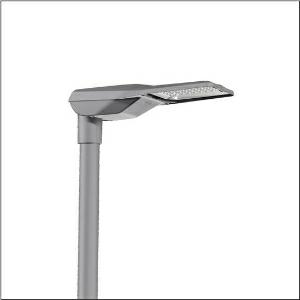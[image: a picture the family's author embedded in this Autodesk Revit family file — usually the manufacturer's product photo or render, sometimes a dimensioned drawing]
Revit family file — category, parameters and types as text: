
# Revit family: streetlight_sl_21_iq_mini___st1_0a_5xe2d31g08hb_3bda
name_source: partatom
category: Lighting Fixtures
units: mm (PartAtom-declared; Revit-internal decimal feet)

## family parameters
Cut with Voids When Loaded = No
Host = Face
Light Source = No
Part Type = Normal
Room Calculation Point = No
Round Connector Dimension = Use Diameter
Shared = No

## types (1)
- --- (1 x LED, 9450 lm, 70.9 W, 3000K)
    Apparent Load = 71 VA
    CIE Flux Codes = 37 72 97 100 100
    Color Rendering = 70
    Color Temperature = 3000K
    Default Elevation = 1800 mm
    Description = Streetlight SL 21 iQ mini, mast luminaire, primary light control with lens, of PMMA, primary optical cover: cover, of toughened safety glass, transparent, light distribution: ST1.0a, light emission: direct distribution, primary light characteristic: asymmetric, installation type: post-top, side-entry, LED, High Power LED, rated luminous flux: 9.450lm, luminous efficacy: 133lm/W, light colour: 730, colour temperature: 3000K, control gear: iQ Street-Remote, control: Street-Remote, Auto-Match, Temp-Guard, Lumen-Switch, Night-Set, Smart-Wire, Light-Fading, Desk-Remote (wireless, voltage-free reading and setting of iQ features in the workshop via application-optimized NFC function/RFID function), optimised constant luminous flux control (CLO 2.0), pre-setting: linear dimming characteristic, mains connection: 220..240V, AC, 50/60Hz, start of lifetime: 71W, end of service life: 75W, reduction: 31W, luminaire housing, of diecast aluminium, powder-coated, Siteco® metallic grey (DB 702S), corrosivity category C5 mid according to DIN EN ISO 12944, please order mast flange separately, inclination adjustable: 0°, 5°, 10°, 15°, sealing non-destructively replaceable, multi-level sealing system, length: 628mm, width: 235mm, height: 110mm, mast flange for spigot size: 42mm (side-entry): 5XC10008XM4, 60/48mm (side-entry/post-top): 5XC10108XM2, 76/60mm (side-entry/post-top): 5XC10108XM1, mounting height: 4..8m, protection rating (complete): IP66, insulation class (complete): insulation class II (safety insulation), certification: CE, ENEC, ENEC+, VDE, impact resistance: IK10, permissible operating ambient temperature for outdoor applications: -40..+50°C, standard-compliant lighting for roads and squares, packaging unit: 1 piece

Light Distribution: ST1.0a
    Height = 110 mm
    Lamp = 1 x LED
    Lamp Light Flux = 9450 lm
    Lamp Power = 70.9 W
    Lamp count = 1
    Length = 625 mm
    Luminous efficacy = 133 lm/W
    Manufacturer = Siteco
    ModVariant = No
    Model = 5XE2D31G08HB
    Number of Poles = 1
    OnlyDefault = Yes
    Power Factor = 1
    Product Name = Streetlight SL 21 iQ mini | ST1.0a
    Product group = mast luminaire | pylon top
    ProductGroupID = 6100
    Protection Class = Protection class II
    Protection Degree = IP 66
    RLX_Detail_Level = 1
    RLX_Emergency_Light_Flux = 0 lm
    RLX_Emergency_Type = 0
    RLX_Emergency_Type_DB = No
    RlxData = <blob elided: 26325 chars, md5=b55f4530>
    Socket = socket
    Standby Power = 0 W
    System Light Flux = 9450 lm
    System Power = 71 W
    Type Comments = factory setting: luminous flux: 100 % | dim-lin: 254 | 711 mA
    Type Image = l_1003519.jpg
    URL = http://relux.com
    VarID = @adj_179591
    Voltage = 0 V
    Weight = 0.00 kg
    Width = 234 mm

## geometry (parser evidence)
native form markers: Blend x4, Sweep x10
no freeform markers — native parametric forms only
